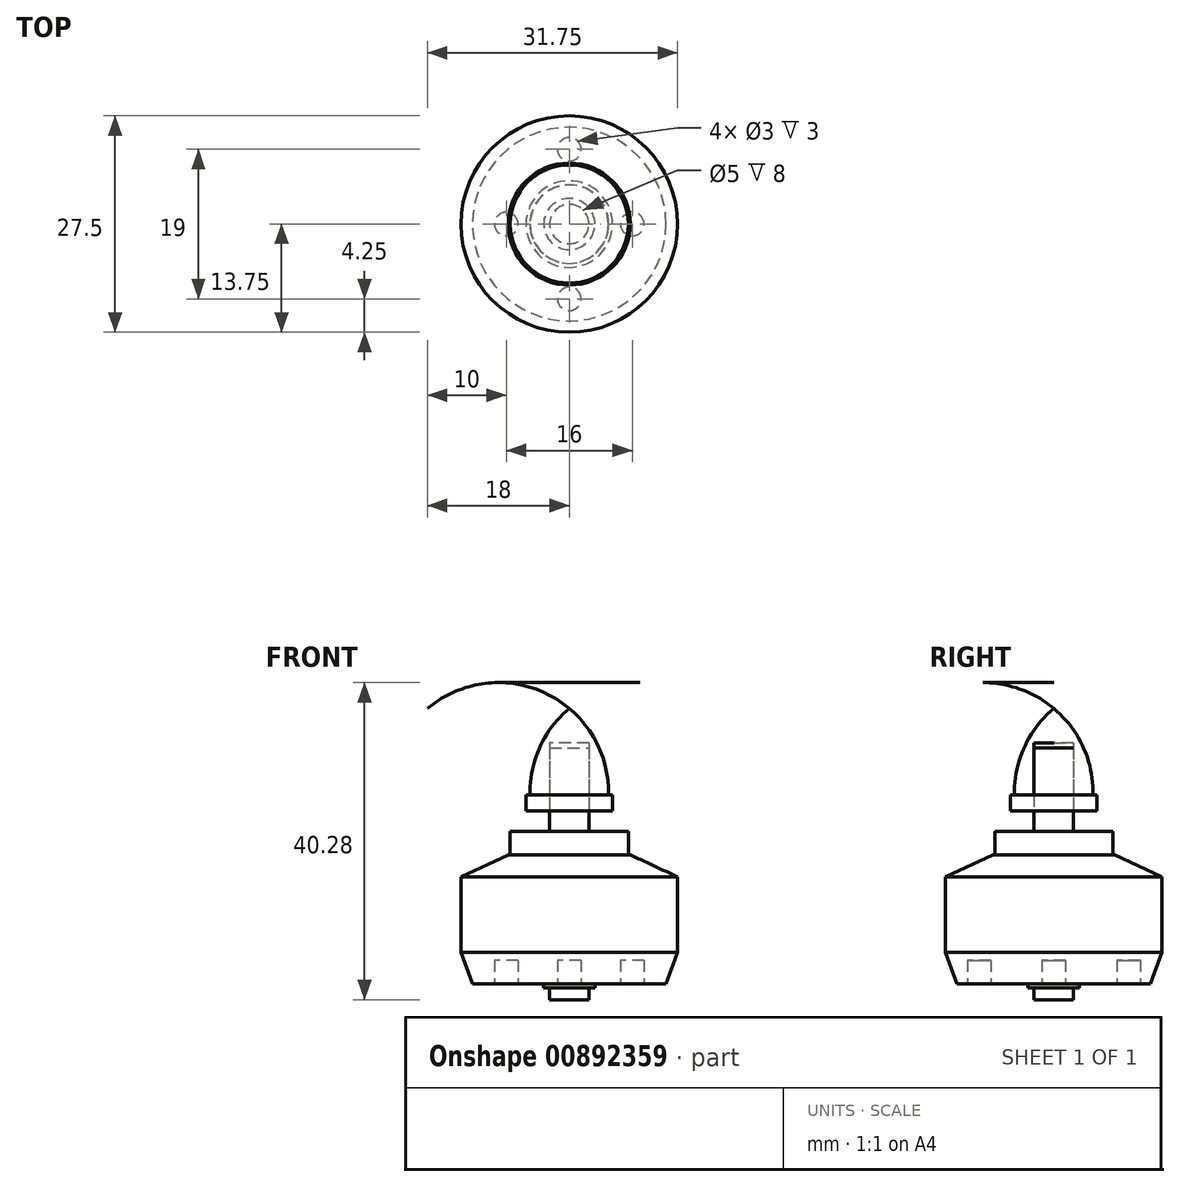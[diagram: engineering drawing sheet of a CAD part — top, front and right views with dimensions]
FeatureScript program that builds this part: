
annotation { "Feature Type Name" : "Feature", "Feature Type Description" : "" }
export const myFeature = defineFeature(function(context is Context, id is Id, definition is map)
    precondition{}
    {
        {
            var Q0;
            Q0=qCreatedBy(makeId("Top.planeOp"),FACE);
            var sketch = newSketch(context, id + "F0", { "sketchPlane" : qUnion([Q0])});
            skCircle(sketch, "E0", {"center": v(0, 0) * mm, "radius": 13.75 * mm});
            skCircle(sketch, "E1", {"center": v(0, 0) * mm, "radius": 7.5 * mm});
            skCircle(sketch, "E2", {"center": v(0, 0) * mm, "radius": 2.5 * mm});
            skLineSegment(sketch, "E3", {"start": v(-29.61, 0) * mm, "end": v(25.95, 0) * mm, "construction": true});
            skCircle(sketch, "E4", {"center": v(-8, 0) * mm, "radius": 1.5 * mm});
            skCircle(sketch, "E5", {"center": v(8, 0) * mm, "radius": 1.5 * mm});
            skCircle(sketch, "E6", {"center": v(0, -9.5) * mm, "radius": 1.5 * mm});
            skCircle(sketch, "E7", {"center": v(0, 9.5) * mm, "radius": 1.5 * mm});
            skCircle(sketch, "E8", {"center": v(0, 0) * mm, "radius": 3.25 * mm});
            skSolve(sketch);
        }
        {
            var Q0;
            Q0=makeQuery(id+"F0.imprint","IMPRINT",FACE,{"disambiguationData":[TD([[makeQuery(id+"F0.imprint","IMPRINT",EDGE,{"derivedFrom":sQuery(id+"F0.wireOp",EDGE,"E0")}),1.0]])]});
            var Q1;
            {var subQ0=sQuery(id+"F0.wireOp",EDGE,"E4");var subQ1=sQuery(id+"F0.wireOp",EDGE,"E1");var subQ2=makeQuery(id+"F0.imprint","INTERSECT",VERTEX,{"disambiguationData":[OD(0.0)],"derivedFrom":[subQ1,subQ0]});Q1=makeQuery(id+"F0.imprint","IMPRINT",FACE,{"disambiguationData":[TD([[makeQuery(id+"F0.imprint","IMPRINT",EDGE,{"disambiguationData":[TD([[subQ2,-1.0]])],"derivedFrom":subQ1}),-1.0]])]});}
            var Q2;
            {var subQ0=sQuery(id+"F0.wireOp",EDGE,"E5");var subQ1=sQuery(id+"F0.wireOp",EDGE,"E1");var subQ2=makeQuery(id+"F0.imprint","INTERSECT",VERTEX,{"disambiguationData":[OD(0.0)],"derivedFrom":[subQ1,subQ0]});Q2=makeQuery(id+"F0.imprint","IMPRINT",FACE,{"disambiguationData":[TD([[makeQuery(id+"F0.imprint","IMPRINT",EDGE,{"disambiguationData":[TD([[subQ2,1.0]])],"derivedFrom":subQ1}),-1.0]])]});}
            var Q3;
            Q3=makeQuery(id+"F0.imprint","IMPRINT",FACE,{"disambiguationData":[TD([[makeQuery(id+"F0.imprint","IMPRINT",EDGE,{"derivedFrom":sQuery(id+"F0.wireOp",EDGE,"E6")}),1.0]])]});
            var Q4;
            Q4=makeQuery(id+"F0.imprint","IMPRINT",FACE,{"disambiguationData":[TD([[makeQuery(id+"F0.imprint","IMPRINT",EDGE,{"derivedFrom":sQuery(id+"F0.wireOp",EDGE,"E7")}),1.0]])]});
            extrude(context, id + "F1", {"entities" : qUnion([Q0, Q1, Q2, Q3, Q4]), "depth" : 16.4 * mm, "offsetDistance" : 25 * mm});
        }
        {
            var Q0;
            Q0=makeQuery(id+"F0.imprint","IMPRINT",FACE,{"disambiguationData":[TD([[makeQuery(id+"F0.imprint","IMPRINT",EDGE,{"derivedFrom":sQuery(id+"F0.wireOp",EDGE,"E1")}),1.0]])]});
            var Q1;
            {var subQ0=sQuery(id+"F0.wireOp",EDGE,"E4");var subQ1=sQuery(id+"F0.wireOp",EDGE,"E1");var subQ2=makeQuery(id+"F0.imprint","INTERSECT",VERTEX,{"disambiguationData":[OD(0.0)],"derivedFrom":[subQ1,subQ0]});Q1=makeQuery(id+"F0.imprint","IMPRINT",FACE,{"disambiguationData":[TD([[makeQuery(id+"F0.imprint","IMPRINT",EDGE,{"disambiguationData":[TD([[subQ2,-1.0]])],"derivedFrom":subQ1}),1.0]])]});}
            var Q2;
            {var subQ0=sQuery(id+"F0.wireOp",EDGE,"E5");var subQ1=sQuery(id+"F0.wireOp",EDGE,"E1");var subQ2=makeQuery(id+"F0.imprint","INTERSECT",VERTEX,{"disambiguationData":[OD(0.0)],"derivedFrom":[subQ1,subQ0]});Q2=makeQuery(id+"F0.imprint","IMPRINT",FACE,{"disambiguationData":[TD([[makeQuery(id+"F0.imprint","IMPRINT",EDGE,{"disambiguationData":[TD([[subQ2,1.0]])],"derivedFrom":subQ1}),1.0]])]});}
            var Q3;
            Q3=makeQuery(id+"F0.imprint","IMPRINT",FACE,{"disambiguationData":[TD([[makeQuery(id+"F0.imprint","IMPRINT",EDGE,{"derivedFrom":sQuery(id+"F0.wireOp",EDGE,"E2")}),-1.0]])]});
            extrude(context, id + "F2", {"entities" : qUnion([Q0, Q1, Q2, Q3]), "operationType" : NewBodyOperationType.ADD, "depth" : 19.4 * mm, "offsetDistance" : 25 * mm});
        }
        {
            var Q0;
            Q0=makeQuery(id+"F0.imprint","IMPRINT",FACE,{"disambiguationData":[TD([[makeQuery(id+"F0.imprint","IMPRINT",EDGE,{"derivedFrom":sQuery(id+"F0.wireOp",EDGE,"E2")}),1.0]])]});
            extrude(context, id + "F3", {"entities" : qUnion([Q0]), "operationType" : NewBodyOperationType.ADD, "depth" : 30.6 * mm, "offsetDistance" : 25 * mm, "hasSecondDirection" : true, "secondDirectionOppositeDirection" : true, "secondDirectionDepth" : 2 * mm});
        }
        {
            var Q0;
            Q0=makeQuery(id+"F0.imprint","IMPRINT",FACE,{"disambiguationData":[TD([[makeQuery(id+"F0.imprint","IMPRINT",EDGE,{"derivedFrom":sQuery(id+"F0.wireOp",EDGE,"E2")}),-1.0]])]});
            extrude(context, id + "F4", {"entities" : qUnion([Q0]), "operationType" : NewBodyOperationType.ADD, "oppositeDirection" : true, "depth" : 0.5 * mm, "offsetDistance" : 25 * mm});
        }
        {
            var Q0;
            Q0=makeQuery(id+"F1.opExtrude","CAP_EDGE",EDGE,{"disambiguationData":[OSD([sQuery(id+"F0.wireOp",EDGE,"E0")])],"isStart":false});
            chamfer(context, id + "F5", {"entities" : qUnion([Q0]), "chamferType" : ChamferType.OFFSET_ANGLE, "width" : 6 * mm, "oppositeDirection" : false, "angle" : 25 * degree, "tangentPropagation" : true});
        }
        {
            var Q0;
            Q0=qCreatedBy(makeId("Top.planeOp"),FACE);
            cPlane(context, id + "F6", {"entities" : qUnion([Q0]), "cplaneType" : CPlaneType.OFFSET, "offset" : 22 * mm, "width" : 150 * mm, "height" : 150 * mm});
        }
        {
            var Q0;
            Q0=qCreatedBy(makeId("Front.planeOp"),FACE);
            var sketch = newSketch(context, id + "F7", { "sketchPlane" : qUnion([Q0])});
            skLineSegment(sketch, "E9", {"start": v(2.5, 22) * mm, "end": v(5.5, 22) * mm});
            skLineSegment(sketch, "E10", {"start": v(5.5, 22) * mm, "end": v(5.5, 24) * mm});
            skLineSegment(sketch, "E11", {"start": v(5.5, 24) * mm, "end": v(5, 24) * mm});
            skArc(sketch, "E12", {"start": v(5, 24) * mm, "mid": v(3.75, 30.07) * mm, "end": v(0, 35) * mm});
            skLineSegment(sketch, "E13", {"start": v(2.5, 22) * mm, "end": v(2.5, 30) * mm});
            skLineSegment(sketch, "E14", {"start": v(2.5, 30) * mm, "end": v(0, 30) * mm});
            skLineSegment(sketch, "E15", {"start": v(0, 0) * mm, "end": v(0, 48.2) * mm, "construction": true});
            skLineSegment(sketch, "E16", {"start": v(0, 30) * mm, "end": v(0, 35) * mm});
            skSolve(sketch);
        }
        {
            var Q0;
            Q0=qSketchRegion(id+"F7",true);
            var Q1;
            Q1=sQuery(id+"F7.wireOp",EDGE,"E15");
            revolve(context, id + "F8", {"surfaceOperationType" : NewSurfaceOperationType.NEW, "entities" : qUnion([Q0]), "axis" : qUnion([Q1]), "revolveType" : RevolveType.FULL});
        }
        {
            var Q0;
            {var subQ0=sQuery(id+"F0.wireOp",EDGE,"E4");var subQ1=sQuery(id+"F0.wireOp",EDGE,"E1");var subQ2=makeQuery(id+"F0.imprint","INTERSECT",VERTEX,{"disambiguationData":[OD(0.0)],"derivedFrom":[subQ1,subQ0]});Q0=makeQuery(id+"F0.imprint","IMPRINT",FACE,{"disambiguationData":[TD([[makeQuery(id+"F0.imprint","IMPRINT",EDGE,{"disambiguationData":[TD([[subQ2,-1.0]])],"derivedFrom":subQ1}),1.0]])]});}
            var Q1;
            {var subQ0=sQuery(id+"F0.wireOp",EDGE,"E4");var subQ1=sQuery(id+"F0.wireOp",EDGE,"E1");var subQ2=makeQuery(id+"F0.imprint","INTERSECT",VERTEX,{"disambiguationData":[OD(0.0)],"derivedFrom":[subQ1,subQ0]});Q1=makeQuery(id+"F0.imprint","IMPRINT",FACE,{"disambiguationData":[TD([[makeQuery(id+"F0.imprint","IMPRINT",EDGE,{"disambiguationData":[TD([[subQ2,-1.0]])],"derivedFrom":subQ1}),-1.0]])]});}
            var Q2;
            Q2=makeQuery(id+"F0.imprint","IMPRINT",FACE,{"disambiguationData":[TD([[makeQuery(id+"F0.imprint","IMPRINT",EDGE,{"derivedFrom":sQuery(id+"F0.wireOp",EDGE,"E6")}),1.0]])]});
            var Q3;
            {var subQ0=sQuery(id+"F0.wireOp",EDGE,"E5");var subQ1=sQuery(id+"F0.wireOp",EDGE,"E1");var subQ2=makeQuery(id+"F0.imprint","INTERSECT",VERTEX,{"disambiguationData":[OD(0.0)],"derivedFrom":[subQ1,subQ0]});Q3=makeQuery(id+"F0.imprint","IMPRINT",FACE,{"disambiguationData":[TD([[makeQuery(id+"F0.imprint","IMPRINT",EDGE,{"disambiguationData":[TD([[subQ2,1.0]])],"derivedFrom":subQ1}),-1.0]])]});}
            var Q4;
            {var subQ0=sQuery(id+"F0.wireOp",EDGE,"E5");var subQ1=sQuery(id+"F0.wireOp",EDGE,"E1");var subQ2=makeQuery(id+"F0.imprint","INTERSECT",VERTEX,{"disambiguationData":[OD(0.0)],"derivedFrom":[subQ1,subQ0]});Q4=makeQuery(id+"F0.imprint","IMPRINT",FACE,{"disambiguationData":[TD([[makeQuery(id+"F0.imprint","IMPRINT",EDGE,{"disambiguationData":[TD([[subQ2,1.0]])],"derivedFrom":subQ1}),1.0]])]});}
            var Q5;
            Q5=makeQuery(id+"F0.imprint","IMPRINT",FACE,{"disambiguationData":[TD([[makeQuery(id+"F0.imprint","IMPRINT",EDGE,{"derivedFrom":sQuery(id+"F0.wireOp",EDGE,"E7")}),1.0]])]});
            extrude(context, id + "F9", {"entities" : qUnion([Q0, Q1, Q2, Q3, Q4, Q5]), "operationType" : NewBodyOperationType.REMOVE, "depth" : 3 * mm, "offsetDistance" : 25 * mm});
        }
        {
            var Q0;
            Q0=makeQuery(id+"F1.opExtrude","CAP_EDGE",EDGE,{"disambiguationData":[OSD([sQuery(id+"F0.wireOp",EDGE,"E0")])],"isStart":true});
            chamfer(context, id + "F10", {"entities" : qUnion([Q0]), "chamferType" : ChamferType.OFFSET_ANGLE, "width" : 4 * mm, "oppositeDirection" : false, "angle" : 20 * degree, "tangentPropagation" : true});
        }
    });
